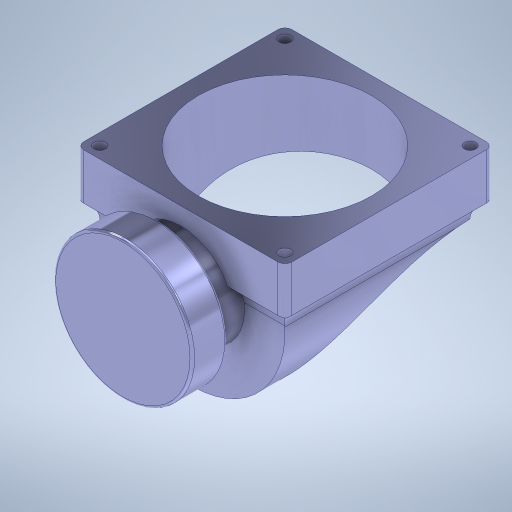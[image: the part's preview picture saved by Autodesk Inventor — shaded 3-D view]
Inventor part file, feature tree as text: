
AUTODESK INVENTOR PART (.ipt)
format: ipt  version: 2023 (Build 270158000, 158)  size: 390,656 bytes
history: native  units: mm
features: extrude x8, sketch x7, other x3, fillet x3
ambient origin geometry x8: Origin, YZ Plane, XZ Plane, XY Plane, X Axis, Y Axis, Z Axis, Center Point
bodies: Body1 (feature_tree)
feature tree (21):
  other  "솔리드1"
  extrude  "돌출1"  Depth=60.0mm
  extrude  "돌출2"  Depth=15.0mm TaperAngle=0.0deg
  extrude  "돌출3"  Depth=45.0mm
  fillet  "모깎기1"  Radius=15.0mm
  other  "작업 평면1"
  sketch  "스케치4"
  extrude  "돌출15"  Depth=80.0mm
  extrude  "돌출16"  Depth=80.0mm TaperAngle=0.0deg
  sketch  "스케치15"
  extrude  "돌출17"  Depth=1.0mm
  extrude  "돌출18"  Depth=5.0mm
  other  "작업 평면10"
  extrude  "돌출19"  Depth=5.0mm
  fillet  "모깎기9"  Radius=5.0mm
  fillet  "모깎기10"  Radius=5.0mm
  sketch  "스케치1"
  sketch  "스케치2"
  sketch  "스케치3"
  sketch  "스케치14"
  sketch  "스케치16"
